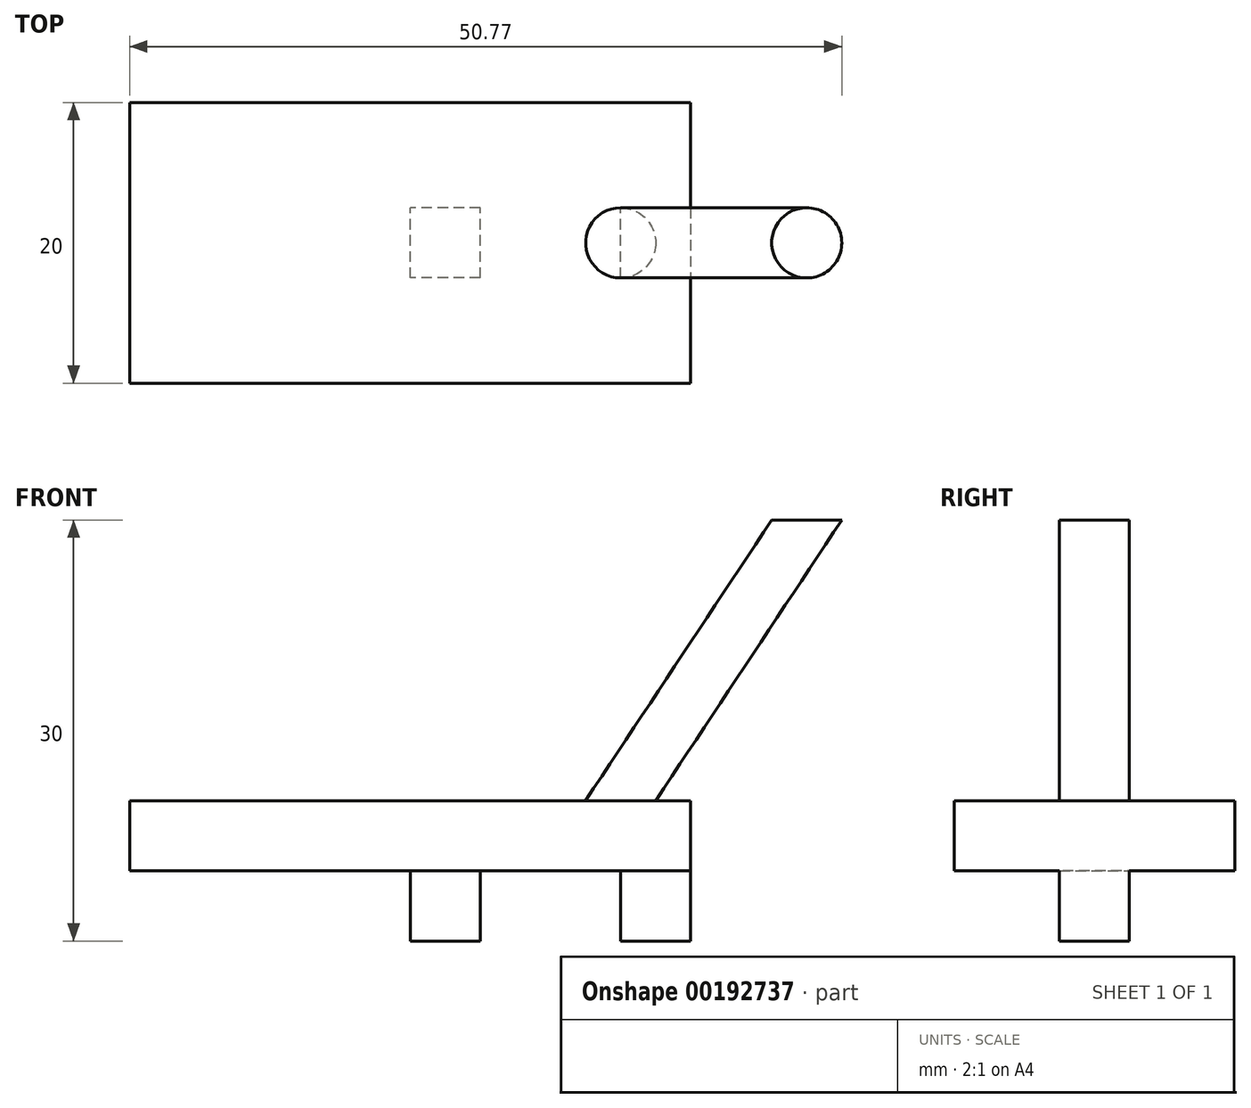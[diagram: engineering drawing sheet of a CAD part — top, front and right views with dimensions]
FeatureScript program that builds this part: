
annotation { "Feature Type Name" : "Feature", "Feature Type Description" : "" }
export const myFeature = defineFeature(function(context is Context, id is Id, definition is map)
    precondition{}
    {
        {
            var Q0;
            Q0=qCreatedBy(makeId("Top.planeOp"),FACE);
            var sketch = newSketch(context, id + "F0", { "sketchPlane" : qUnion([Q0])});
            skLineSegment(sketch, "E0.bottom", {"start": v(20, 10) * mm, "end": v(-20, 10) * mm});
            skLineSegment(sketch, "E0.top", {"start": v(20, -10) * mm, "end": v(-20, -10) * mm});
            skLineSegment(sketch, "E0.left", {"start": v(20, 10) * mm, "end": v(20, -10) * mm});
            skLineSegment(sketch, "E0.right", {"start": v(-20, 10) * mm, "end": v(-20, -10) * mm});
            skPoint(sketch, "E0.middle", {"position": v(0, 0) * mm});
            skSolve(sketch);
        }
        {
            var Q0;
            Q0 = qSketchRegion(id + "F0", true);
            extrude(context, id + "F1", {"entities" : qUnion([Q0]), "depth" : 5 * mm});
        }
        {
            var Q0;
            Q0=makeQuery(id+"F1.opExtrude","CAP_FACE",FACE,{"disambiguationData":[OSD([sQuery(id+"F0.wireOp",EDGE,"E0.bottom"),sQuery(id+"F0.wireOp",EDGE,"E0.top"),sQuery(id+"F0.wireOp",EDGE,"E0.left"),sQuery(id+"F0.wireOp",EDGE,"E0.right")])],"isStart":true});
            var sketch = newSketch(context, id + "F2", { "sketchPlane" : qUnion([Q0])});
            skLineSegment(sketch, "E1", {"start": v(20, 2.5) * mm, "end": v(15, 2.5) * mm});
            skLineSegment(sketch, "E2", {"start": v(15, 2.5) * mm, "end": v(15, -2.5) * mm});
            skLineSegment(sketch, "E3", {"start": v(15, -2.5) * mm, "end": v(20, -2.5) * mm});
            skLineSegment(sketch, "E4", {"start": v(20, -2.5) * mm, "end": v(20, 0) * mm});
            skLineSegment(sketch, "E5", {"start": v(20, 0) * mm, "end": v(20, 2.5) * mm});
            skLineSegment(sketch, "E6.bottom", {"start": v(5, 2.5) * mm, "end": v(0, 2.5) * mm});
            skLineSegment(sketch, "E6.top", {"start": v(5, -2.5) * mm, "end": v(0, -2.5) * mm});
            skLineSegment(sketch, "E6.left", {"start": v(5, 2.5) * mm, "end": v(5, -2.5) * mm});
            skLineSegment(sketch, "E6.right", {"start": v(0, 2.5) * mm, "end": v(0, -2.5) * mm});
            skPoint(sketch, "E6.middle", {"position": v(2.5, 0) * mm});
            skSolve(sketch);
        }
        {
            var Q0;
            Q0 = qSketchRegion(id + "F2", true);
            extrude(context, id + "F3", {"entities" : qUnion([Q0]), "operationType" : NewBodyOperationType.ADD, "depth" : 5 * mm});
        }
        {
            var Q0;
            Q0=makeQuery(id+"F1.opExtrude","CAP_FACE",FACE,{"disambiguationData":[OSD([sQuery(id+"F0.wireOp",EDGE,"E0.bottom"),sQuery(id+"F0.wireOp",EDGE,"E0.top"),sQuery(id+"F0.wireOp",EDGE,"E0.left"),sQuery(id+"F0.wireOp",EDGE,"E0.right")])],"isStart":false});
            var sketch = newSketch(context, id + "F4", { "sketchPlane" : qUnion([Q0])});
            skCircle(sketch, "E7", {"center": v(15, 0) * mm, "radius": 2.5 * mm});
            skSolve(sketch);
        }
        {
            var Q0;
            Q0=makeQuery(id+"F1.opExtrude","SWEPT_FACE",FACE,{"disambiguationData":[OSD([sQuery(id+"F0.wireOp",EDGE,"E0.top")])]});
            var sketch = newSketch(context, id + "F5", { "sketchPlane" : qUnion([Q0])});
            skLineSegment(sketch, "E8", {"start": v(0, 0) * mm, "end": v(16.58, 25) * mm});
            skSolve(sketch);
        }
        {
            var Q0;
            Q0=makeQuery(id+"F4.imprint","IMPRINT",FACE,{"disambiguationData":[TD([[makeQuery(id+"F4.imprint","IMPRINT",EDGE,{"derivedFrom":sQuery(id+"F4.wireOp",EDGE,"E7")}),1.0]])]});
            var Q1;
            Q1=sQuery(id+"F5.wireOp",EDGE,"E8");
            sweep(context, id + "F6", {"operationType" : NewBodyOperationType.ADD, "profiles" : qUnion([Q0]), "path" : qUnion([Q1])});
        }
    });
